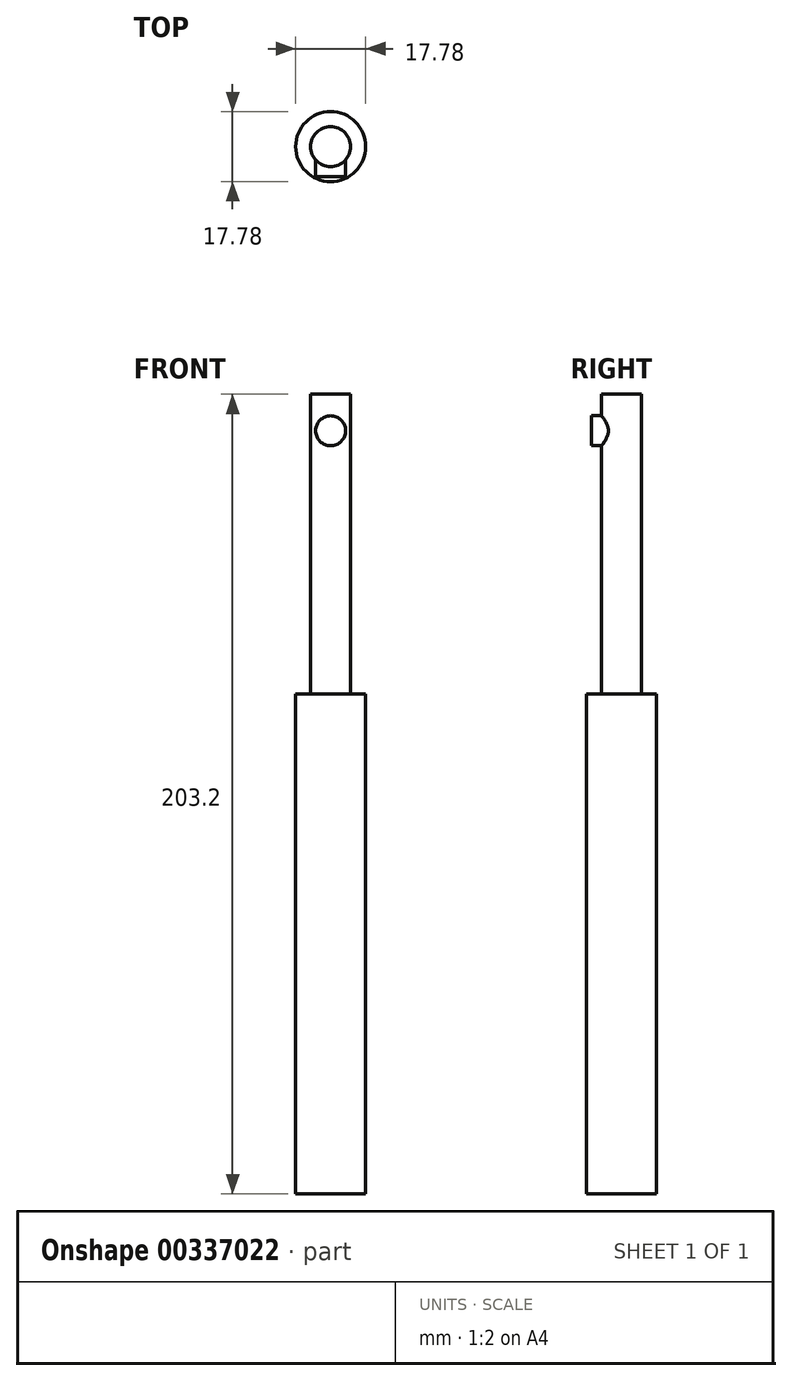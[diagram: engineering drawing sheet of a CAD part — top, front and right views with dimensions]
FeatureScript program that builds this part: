
annotation { "Feature Type Name" : "Feature", "Feature Type Description" : "" }
export const myFeature = defineFeature(function(context is Context, id is Id, definition is map)
    precondition{}
    {
        {
            var Q0;
            Q0=qCreatedBy(makeId("Top.planeOp"),FACE);
            var sketch = newSketch(context, id + "F0", { "sketchPlane" : qUnion([Q0])});
            skCircle(sketch, "E0", {"center": v(0, 0) * mm, "radius": 8.9 * mm});
            skSolve(sketch);
        }
        {
            var Q0;
            Q0 = qSketchRegion(id + "F0", true);
            extrude(context, id + "F1", {"entities" : qUnion([Q0]), "oppositeDirection" : true, "depth" : 127 * mm});
        }
        {
            var Q0;
            Q0=qCreatedBy(makeId("Top.planeOp"),FACE);
            var sketch = newSketch(context, id + "F2", { "sketchPlane" : qUnion([Q0])});
            skCircle(sketch, "E1", {"center": v(0, 0) * mm, "radius": 5.08 * mm});
            skSolve(sketch);
        }
        {
            var Q0;
            Q0 = qSketchRegion(id + "F2", true);
            extrude(context, id + "F3", {"entities" : qUnion([Q0]), "operationType" : NewBodyOperationType.ADD, "depth" : 76.2 * mm});
        }
        {
            var Q0;
            Q0=qCreatedBy(makeId("Front.planeOp"),FACE);
            var sketch = newSketch(context, id + "F4", { "sketchPlane" : qUnion([Q0])});
            skCircle(sketch, "E2", {"center": v(0, 66.9) * mm, "radius": 3.81 * mm});
            skSolve(sketch);
        }
        {
            var Q0;
            Q0 = qSketchRegion(id + "F4", true);
            extrude(context, id + "F5", {"entities" : qUnion([Q0]), "operationType" : NewBodyOperationType.ADD, "depth" : 7.62 * mm});
        }
    });
